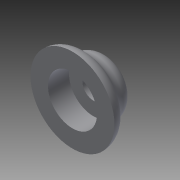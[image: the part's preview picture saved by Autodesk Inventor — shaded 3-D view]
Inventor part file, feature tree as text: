
AUTODESK INVENTOR PART (.ipt)
format: ipt  version: 2014 (Build 180170000, 170)  size: 181,248 bytes
history: native  units: mm
features: extrude x4, sketch x4, fillet x1
ambient origin geometry x8: Origin, YZ Plane, XZ Plane, XY Plane, X Axis, Y Axis, Z Axis, Center Point
bodies: Solid1 (feature_tree)
feature tree (9):
  extrude  "Extrusion1"  Depth=5.2mm
  extrude  "Extrusion2"  Depth=10.0mm TaperAngle=0.0deg
  extrude  "Extrusion3"  Depth=14.0mm
  extrude  "Extrusion4"  Depth=24.0mm
  fillet  "Fillet1"  Radius=3.0mm
  sketch  "Sketch1"  dims[d0=6.3mm d1=5.2mm]
  sketch  "Sketch2"  dims[d2=16.0mm d3=10.0mm d4=0.0mm]
  sketch  "Sketch3"  dims[d5=1.0mm d6=0.0mm d7=14.0mm]
  sketch  "Sketch4"  dims[d8=6.0mm d9=0.0mm d10=24.0mm d11=3.0mm d12=0.0mm d13=4.0mm]
